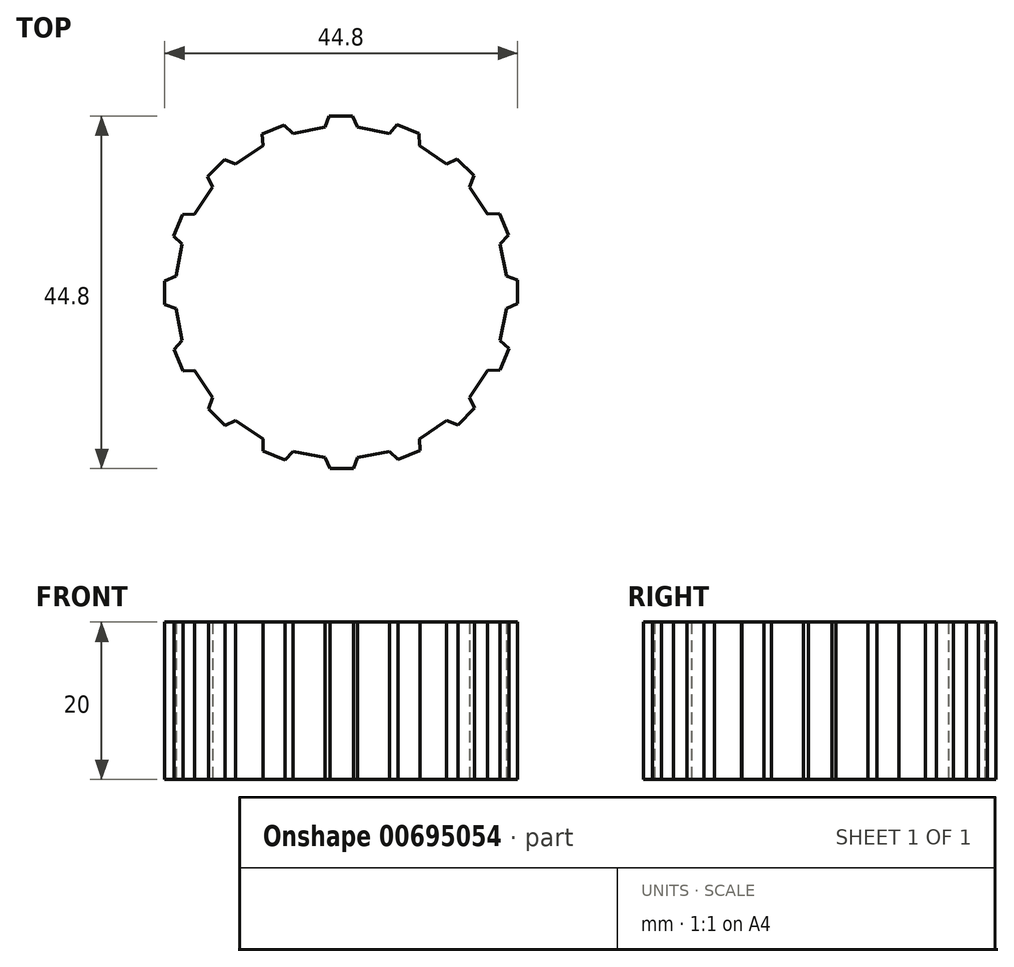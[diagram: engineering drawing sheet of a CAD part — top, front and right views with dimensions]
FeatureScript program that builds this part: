
annotation { "Feature Type Name" : "Feature", "Feature Type Description" : "" }
export const myFeature = defineFeature(function(context is Context, id is Id, definition is map)
    precondition{}
    {
        {
            var Q0;
            Q0=qCreatedBy(makeId("Top.planeOp"),FACE);
            var sketch = newSketch(context, id + "F0", { "sketchPlane" : qUnion([Q0])});
            skCircle(sketch, "E0.cCircle", {"center": v(0, 0) * mm, "radius": 21 * mm, "construction": true});
            skLineSegment(sketch, "E0.0", {"start": v(21, 2.07) * mm, "end": v(21, -2.07) * mm});
            skLineSegment(sketch, "E0.1", {"start": v(21, -2.07) * mm, "end": v(20.2, -6.13) * mm});
            skLineSegment(sketch, "E0.2", {"start": v(20.2, -6.13) * mm, "end": v(18.6, -9.95) * mm});
            skLineSegment(sketch, "E0.3", {"start": v(18.6, -9.95) * mm, "end": v(16.31, -13.39) * mm});
            skLineSegment(sketch, "E0.4", {"start": v(16.31, -13.39) * mm, "end": v(13.39, -16.31) * mm});
            skLineSegment(sketch, "E0.5", {"start": v(13.39, -16.31) * mm, "end": v(9.95, -18.6) * mm});
            skLineSegment(sketch, "E0.6", {"start": v(9.95, -18.6) * mm, "end": v(6.13, -20.2) * mm});
            skLineSegment(sketch, "E0.7", {"start": v(6.13, -20.2) * mm, "end": v(2.07, -21) * mm});
            skLineSegment(sketch, "E0.8", {"start": v(2.07, -21) * mm, "end": v(-2.07, -21) * mm});
            skLineSegment(sketch, "E0.9", {"start": v(-2.07, -21) * mm, "end": v(-6.13, -20.2) * mm});
            skLineSegment(sketch, "E0.10", {"start": v(-6.13, -20.2) * mm, "end": v(-9.95, -18.6) * mm});
            skLineSegment(sketch, "E0.11", {"start": v(-9.95, -18.6) * mm, "end": v(-13.39, -16.31) * mm});
            skLineSegment(sketch, "E0.12", {"start": v(-13.39, -16.31) * mm, "end": v(-16.31, -13.39) * mm});
            skLineSegment(sketch, "E0.13", {"start": v(-16.31, -13.39) * mm, "end": v(-18.6, -9.95) * mm});
            skLineSegment(sketch, "E0.14", {"start": v(-18.6, -9.95) * mm, "end": v(-20.2, -6.13) * mm});
            skLineSegment(sketch, "E0.15", {"start": v(-20.2, -6.13) * mm, "end": v(-21, -2.07) * mm});
            skLineSegment(sketch, "E0.16", {"start": v(-21, -2.07) * mm, "end": v(-21, 2.07) * mm});
            skLineSegment(sketch, "E0.17", {"start": v(-21, 2.07) * mm, "end": v(-20.2, 6.13) * mm});
            skLineSegment(sketch, "E0.18", {"start": v(-20.2, 6.13) * mm, "end": v(-18.6, 9.95) * mm});
            skLineSegment(sketch, "E0.19", {"start": v(-18.6, 9.95) * mm, "end": v(-16.31, 13.39) * mm});
            skLineSegment(sketch, "E0.20", {"start": v(-16.31, 13.39) * mm, "end": v(-13.39, 16.31) * mm});
            skLineSegment(sketch, "E0.21", {"start": v(-13.39, 16.31) * mm, "end": v(-9.95, 18.6) * mm});
            skLineSegment(sketch, "E0.22", {"start": v(-9.95, 18.6) * mm, "end": v(-6.13, 20.2) * mm});
            skLineSegment(sketch, "E0.23", {"start": v(-6.13, 20.2) * mm, "end": v(-2.07, 21) * mm});
            skLineSegment(sketch, "E0.24", {"start": v(-2.07, 21) * mm, "end": v(2.07, 21) * mm});
            skLineSegment(sketch, "E0.25", {"start": v(2.07, 21) * mm, "end": v(6.13, 20.2) * mm});
            skLineSegment(sketch, "E0.26", {"start": v(6.13, 20.2) * mm, "end": v(9.95, 18.6) * mm});
            skLineSegment(sketch, "E0.27", {"start": v(9.95, 18.6) * mm, "end": v(13.39, 16.31) * mm});
            skLineSegment(sketch, "E0.28", {"start": v(13.39, 16.31) * mm, "end": v(16.31, 13.39) * mm});
            skLineSegment(sketch, "E0.29", {"start": v(16.31, 13.39) * mm, "end": v(18.6, 9.95) * mm});
            skLineSegment(sketch, "E0.30", {"start": v(18.6, 9.95) * mm, "end": v(20.2, 6.13) * mm});
            skLineSegment(sketch, "E0.31", {"start": v(20.2, 6.13) * mm, "end": v(21, 2.07) * mm});
            skPoint(sketch, "E0.0.midPoint", {"position": v(21, 0) * mm});
            skLineSegment(sketch, "E1", {"start": v(-1.57, 22.4) * mm, "end": v(1.43, 22.4) * mm});
            skLineSegment(sketch, "E2", {"start": v(-1.57, 22.4) * mm, "end": v(-2.07, 21) * mm});
            skLineSegment(sketch, "E3", {"start": v(1.43, 22.4) * mm, "end": v(2.07, 21) * mm});
            skLineSegment(sketch, "E4.1.0", {"start": v(7.12, 21.3) * mm, "end": v(6.13, 20.2) * mm});
            skLineSegment(sketch, "E4.1.1", {"start": v(7.12, 21.3) * mm, "end": v(9.9, 20.15) * mm});
            skLineSegment(sketch, "E4.1.2", {"start": v(9.9, 20.15) * mm, "end": v(9.95, 18.6) * mm});
            skLineSegment(sketch, "E4.2.0", {"start": v(14.73, 16.95) * mm, "end": v(13.39, 16.31) * mm});
            skLineSegment(sketch, "E4.2.1", {"start": v(14.73, 16.95) * mm, "end": v(16.85, 14.83) * mm});
            skLineSegment(sketch, "E4.2.2", {"start": v(16.85, 14.83) * mm, "end": v(16.31, 13.39) * mm});
            skLineSegment(sketch, "E4.3.0", {"start": v(20.1, 10.02) * mm, "end": v(18.6, 9.95) * mm});
            skLineSegment(sketch, "E4.3.1", {"start": v(20.1, 10.02) * mm, "end": v(21.24, 7.25) * mm});
            skLineSegment(sketch, "E4.3.2", {"start": v(21.24, 7.25) * mm, "end": v(20.2, 6.13) * mm});
            skLineSegment(sketch, "E4.4.0", {"start": v(22.4, 1.57) * mm, "end": v(21, 2.07) * mm});
            skLineSegment(sketch, "E4.4.1", {"start": v(22.4, 1.57) * mm, "end": v(22.4, -1.43) * mm});
            skLineSegment(sketch, "E4.4.2", {"start": v(22.4, -1.43) * mm, "end": v(21, -2.07) * mm});
            skLineSegment(sketch, "E4.5.0", {"start": v(21.3, -7.12) * mm, "end": v(20.2, -6.13) * mm});
            skLineSegment(sketch, "E4.5.1", {"start": v(21.3, -7.12) * mm, "end": v(20.15, -9.9) * mm});
            skLineSegment(sketch, "E4.5.2", {"start": v(20.15, -9.9) * mm, "end": v(18.6, -9.95) * mm});
            skLineSegment(sketch, "E4.6.0", {"start": v(16.95, -14.73) * mm, "end": v(16.31, -13.39) * mm});
            skLineSegment(sketch, "E4.6.1", {"start": v(16.95, -14.73) * mm, "end": v(14.83, -16.85) * mm});
            skLineSegment(sketch, "E4.6.2", {"start": v(14.83, -16.85) * mm, "end": v(13.39, -16.31) * mm});
            skLineSegment(sketch, "E4.7.0", {"start": v(10.02, -20.1) * mm, "end": v(9.95, -18.6) * mm});
            skLineSegment(sketch, "E4.7.1", {"start": v(10.02, -20.1) * mm, "end": v(7.25, -21.24) * mm});
            skLineSegment(sketch, "E4.7.2", {"start": v(7.25, -21.24) * mm, "end": v(6.13, -20.2) * mm});
            skLineSegment(sketch, "E4.8.0", {"start": v(1.57, -22.4) * mm, "end": v(2.07, -21) * mm});
            skLineSegment(sketch, "E4.8.1", {"start": v(1.57, -22.4) * mm, "end": v(-1.43, -22.4) * mm});
            skLineSegment(sketch, "E4.8.2", {"start": v(-1.43, -22.4) * mm, "end": v(-2.07, -21) * mm});
            skLineSegment(sketch, "E4.9.0", {"start": v(-7.12, -21.3) * mm, "end": v(-6.13, -20.2) * mm});
            skLineSegment(sketch, "E4.9.1", {"start": v(-7.12, -21.3) * mm, "end": v(-9.9, -20.15) * mm});
            skLineSegment(sketch, "E4.9.2", {"start": v(-9.9, -20.15) * mm, "end": v(-9.95, -18.6) * mm});
            skLineSegment(sketch, "E4.10.0", {"start": v(-14.73, -16.95) * mm, "end": v(-13.39, -16.31) * mm});
            skLineSegment(sketch, "E4.10.1", {"start": v(-14.73, -16.95) * mm, "end": v(-16.85, -14.83) * mm});
            skLineSegment(sketch, "E4.10.2", {"start": v(-16.85, -14.83) * mm, "end": v(-16.31, -13.39) * mm});
            skLineSegment(sketch, "E4.11.0", {"start": v(-20.1, -10.02) * mm, "end": v(-18.6, -9.95) * mm});
            skLineSegment(sketch, "E4.11.1", {"start": v(-20.1, -10.02) * mm, "end": v(-21.24, -7.25) * mm});
            skLineSegment(sketch, "E4.11.2", {"start": v(-21.24, -7.25) * mm, "end": v(-20.2, -6.13) * mm});
            skLineSegment(sketch, "E4.12.0", {"start": v(-22.4, -1.57) * mm, "end": v(-21, -2.07) * mm});
            skLineSegment(sketch, "E4.12.1", {"start": v(-22.4, -1.57) * mm, "end": v(-22.4, 1.43) * mm});
            skLineSegment(sketch, "E4.12.2", {"start": v(-22.4, 1.43) * mm, "end": v(-21, 2.07) * mm});
            skLineSegment(sketch, "E4.13.0", {"start": v(-21.3, 7.12) * mm, "end": v(-20.2, 6.13) * mm});
            skLineSegment(sketch, "E4.13.1", {"start": v(-21.3, 7.12) * mm, "end": v(-20.15, 9.9) * mm});
            skLineSegment(sketch, "E4.13.2", {"start": v(-20.15, 9.9) * mm, "end": v(-18.6, 9.95) * mm});
            skLineSegment(sketch, "E4.14.0", {"start": v(-16.95, 14.73) * mm, "end": v(-16.31, 13.39) * mm});
            skLineSegment(sketch, "E4.14.1", {"start": v(-16.95, 14.73) * mm, "end": v(-14.83, 16.85) * mm});
            skLineSegment(sketch, "E4.14.2", {"start": v(-14.83, 16.85) * mm, "end": v(-13.39, 16.31) * mm});
            skLineSegment(sketch, "E4.15.0", {"start": v(-10.02, 20.1) * mm, "end": v(-9.95, 18.6) * mm});
            skLineSegment(sketch, "E4.15.1", {"start": v(-10.02, 20.1) * mm, "end": v(-7.25, 21.24) * mm});
            skLineSegment(sketch, "E4.15.2", {"start": v(-7.25, 21.24) * mm, "end": v(-6.13, 20.2) * mm});
            skLineSegment(sketch, "E4.anchor1", {"start": v(0, 0) * mm, "end": v(-2.07, 21) * mm, "construction": true});
            skLineSegment(sketch, "E4.anchor2", {"start": v(0, 0) * mm, "end": v(-9.95, 18.6) * mm, "construction": true});
            skSolve(sketch);
        }
        {
            var Q0;
            Q0 = qSketchRegion(id + "F0", true);
            extrude(context, id + "F1", {"entities" : qUnion([Q0]), "depth" : 20 * mm, "offsetDistance" : 25 * mm});
        }
    });
